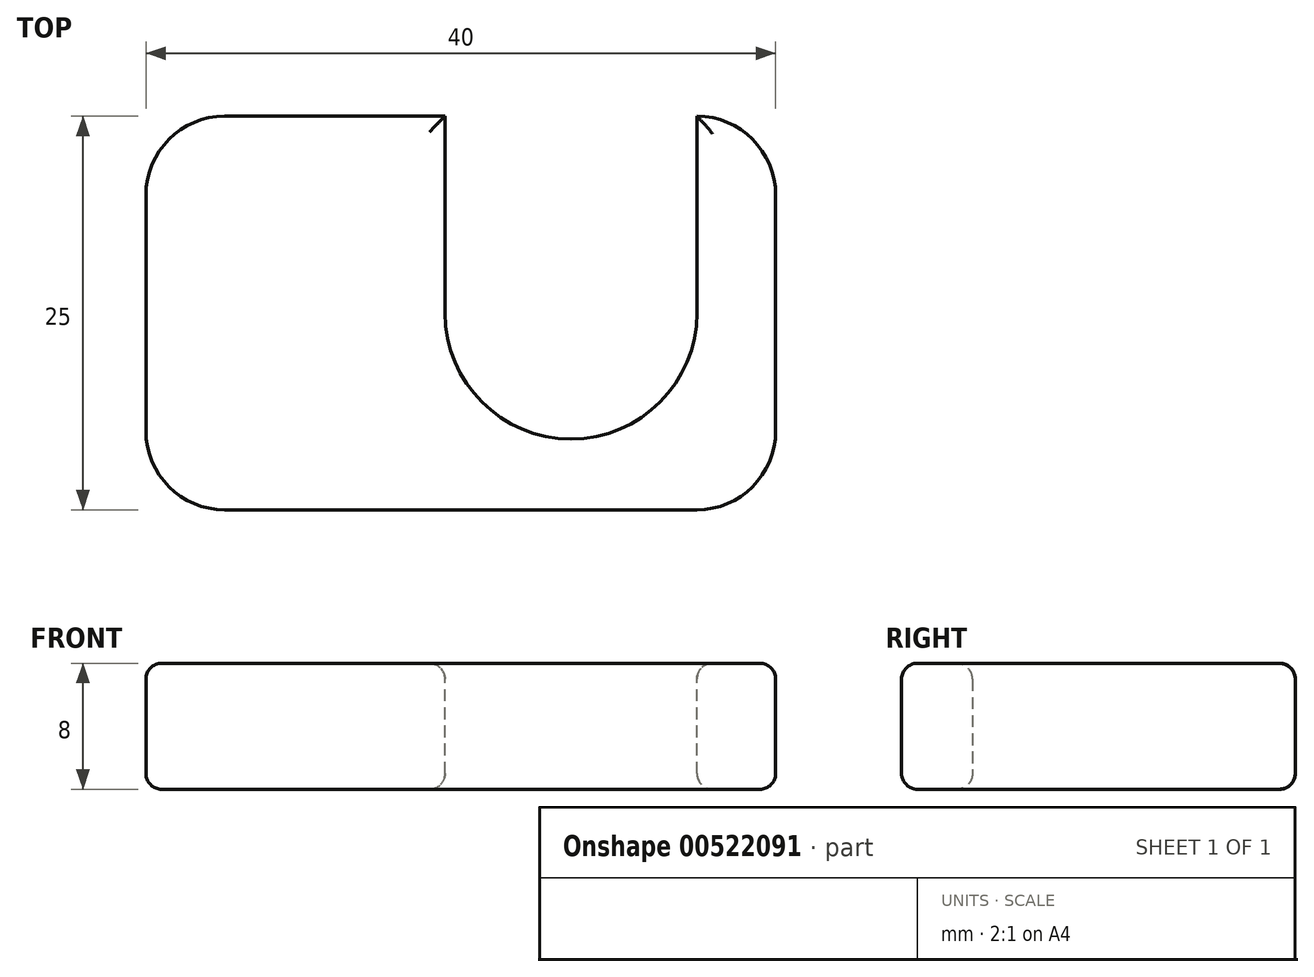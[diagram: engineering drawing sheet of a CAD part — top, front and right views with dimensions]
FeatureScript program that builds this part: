
annotation { "Feature Type Name" : "Feature", "Feature Type Description" : "" }
export const myFeature = defineFeature(function(context is Context, id is Id, definition is map)
    precondition{}
    {
        {
            var Q0;
            Q0=qCreatedBy(makeId("Top.planeOp"),FACE);
            var sketch = newSketch(context, id + "F0", { "sketchPlane" : qUnion([Q0])});
            skLineSegment(sketch, "E0.bottom", {"start": v(20, 12.5) * mm, "end": v(-20, 12.5) * mm});
            skLineSegment(sketch, "E0.top", {"start": v(20, -12.5) * mm, "end": v(-20, -12.5) * mm});
            skLineSegment(sketch, "E0.left", {"start": v(20, 12.5) * mm, "end": v(20, -12.5) * mm});
            skLineSegment(sketch, "E0.right", {"start": v(-20, 12.5) * mm, "end": v(-20, -12.5) * mm});
            skPoint(sketch, "E0.middle", {"position": v(0, 0) * mm});
            skCircle(sketch, "E1", {"center": v(7, 0) * mm, "radius": 8 * mm});
            skSolve(sketch);
        }
        {
            var Q0;
            Q0=makeQuery(id+"F0.imprint","IMPRINT",FACE,{"disambiguationData":[TD([[makeQuery(id+"F0.imprint","IMPRINT",EDGE,{"derivedFrom":sQuery(id+"F0.wireOp",EDGE,"E0.bottom")}),1.0]])]});
            extrude(context, id + "F1", {"entities" : qUnion([Q0]), "depth" : 8 * mm, "offsetDistance" : 25 * mm});
        }
        {
            var Q0;
            Q0=makeQuery(id+"F1.opExtrude","CAP_FACE",FACE,{"disambiguationData":[OSD([sQuery(id+"F0.wireOp",EDGE,"E0.bottom"),sQuery(id+"F0.wireOp",EDGE,"E0.top"),sQuery(id+"F0.wireOp",EDGE,"E0.left"),sQuery(id+"F0.wireOp",EDGE,"E0.right"),sQuery(id+"F0.wireOp",EDGE,"E1")])],"isStart":false});
            var sketch = newSketch(context, id + "F2", { "sketchPlane" : qUnion([Q0])});
            skLineSegment(sketch, "E2.bottom", {"start": v(-1, 0) * mm, "end": v(15, 0) * mm});
            skLineSegment(sketch, "E2.top", {"start": v(-1, 12.5) * mm, "end": v(15, 12.5) * mm});
            skLineSegment(sketch, "E2.left", {"start": v(-1, 0) * mm, "end": v(-1, 12.5) * mm});
            skLineSegment(sketch, "E2.right", {"start": v(15, 0) * mm, "end": v(15, 12.5) * mm});
            skSolve(sketch);
        }
        {
            var Q0;
            Q0=makeQuery(id+"F2.imprint","IMPRINT",FACE,{"disambiguationData":[TD([[makeQuery(id+"F2.imprint","IMPRINT",EDGE,{"derivedFrom":sQuery(id+"F2.wireOp",EDGE,"E2.top")}),1.0]])]});
            extrude(context, id + "F3", {"entities" : qUnion([Q0]), "operationType" : NewBodyOperationType.REMOVE, "endBound" : BoundingType.UP_TO_NEXT, "oppositeDirection" : true, "depth" : 25 * mm, "offsetDistance" : 25 * mm});
        }
        {
            var Q0;
            Q0=makeQuery(id+"F1.opExtrude","SWEPT_EDGE",EDGE,{"disambiguationData":[OSD([sQuery(id+"F0.wireOp",EDGE,"E0.bottom"),sQuery(id+"F0.wireOp",EDGE,"E0.right")])]});
            var Q1;
            Q1=makeQuery(id+"F1.opExtrude","SWEPT_EDGE",EDGE,{"disambiguationData":[OSD([sQuery(id+"F0.wireOp",EDGE,"E0.top"),sQuery(id+"F0.wireOp",EDGE,"E0.right")])]});
            var Q2;
            Q2=makeQuery(id+"F1.opExtrude","SWEPT_EDGE",EDGE,{"disambiguationData":[OSD([sQuery(id+"F0.wireOp",EDGE,"E0.top"),sQuery(id+"F0.wireOp",EDGE,"E0.left")])]});
            var Q3;
            Q3=makeQuery(id+"F1.opExtrude","SWEPT_EDGE",EDGE,{"disambiguationData":[OSD([sQuery(id+"F0.wireOp",EDGE,"E0.bottom"),sQuery(id+"F0.wireOp",EDGE,"E0.left")])]});
            fillet(context, id + "F4", {"entities" : qUnion([Q0, Q1, Q2, Q3]), "radius" : 5 * mm, "tangentPropagation" : true, "allowEdgeOverflow" : false});
        }
        {
            var Q0;
            Q0=makeQuery(id+"F1.opExtrude","CAP_FACE",FACE,{"disambiguationData":[OSD([sQuery(id+"F0.wireOp",EDGE,"E0.bottom"),sQuery(id+"F0.wireOp",EDGE,"E0.top"),sQuery(id+"F0.wireOp",EDGE,"E0.left"),sQuery(id+"F0.wireOp",EDGE,"E0.right"),sQuery(id+"F0.wireOp",EDGE,"E1")])],"isStart":false});
            var Q1;
            Q1=makeQuery(id+"F1.opExtrude","CAP_FACE",FACE,{"disambiguationData":[OSD([sQuery(id+"F0.wireOp",EDGE,"E0.bottom"),sQuery(id+"F0.wireOp",EDGE,"E0.top"),sQuery(id+"F0.wireOp",EDGE,"E0.left"),sQuery(id+"F0.wireOp",EDGE,"E0.right"),sQuery(id+"F0.wireOp",EDGE,"E1")])],"isStart":true});
            fillet(context, id + "F5", {"entities" : qUnion([Q0, Q1]), "radius" : 1 * mm, "tangentPropagation" : true, "allowEdgeOverflow" : false});
        }
    });
